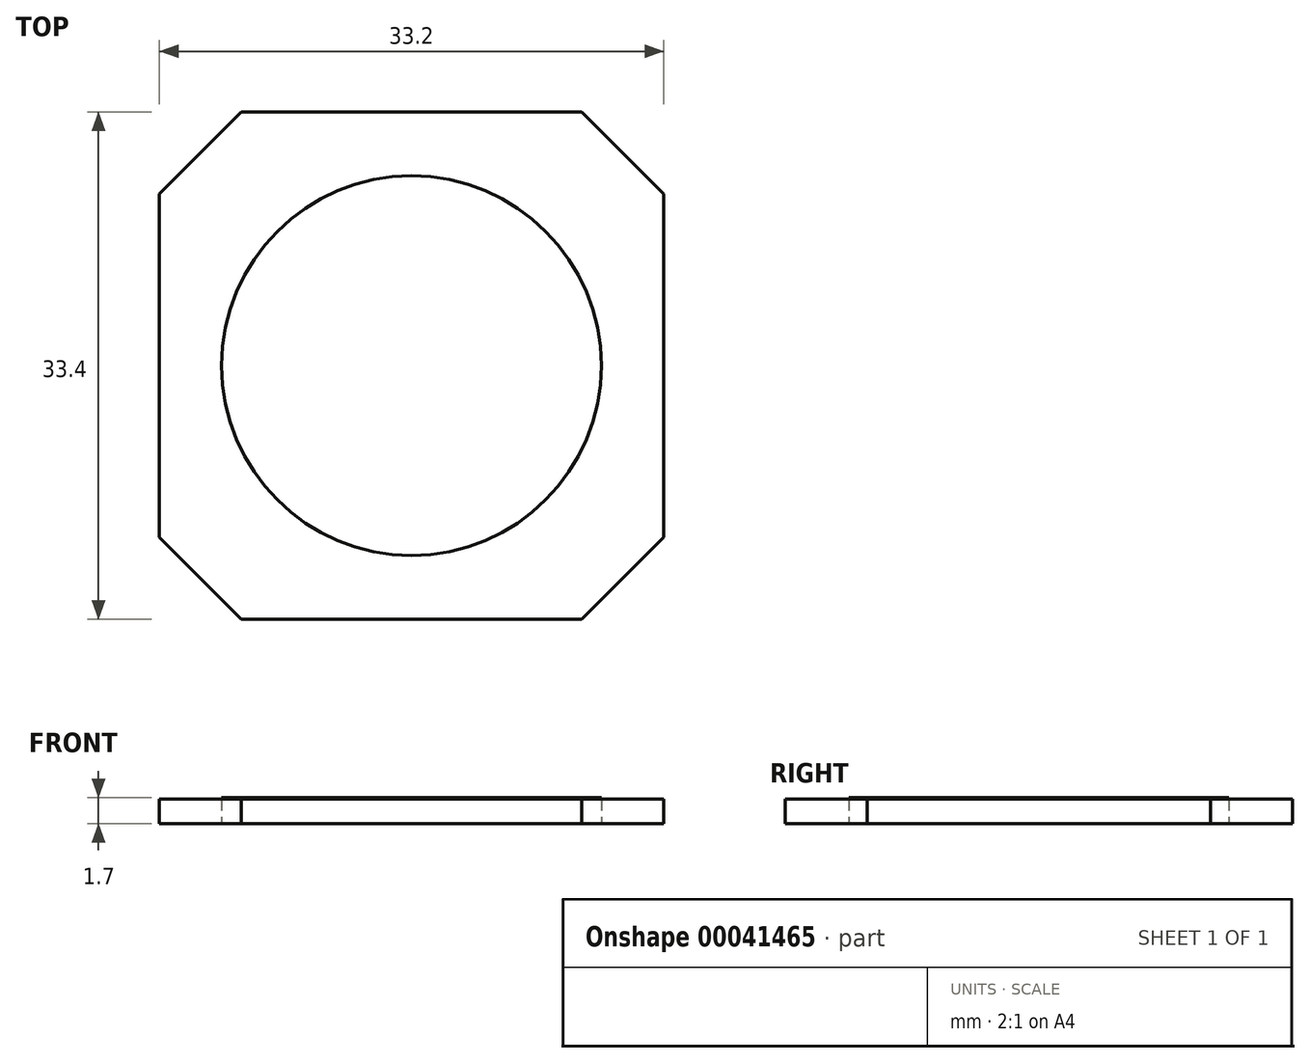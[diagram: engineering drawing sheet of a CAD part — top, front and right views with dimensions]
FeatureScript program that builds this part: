
annotation { "Feature Type Name" : "Feature", "Feature Type Description" : "" }
export const myFeature = defineFeature(function(context is Context, id is Id, definition is map)
    precondition{}
    {
        {
            var Q0;
            Q0=qCreatedBy(makeId("Top.planeOp"),FACE);
            var sketch = newSketch(context, id + "F0", { "sketchPlane" : qUnion([Q0])});
            skCircle(sketch, "E0", {"center": v(0, 0) * mm, "radius": 12.5 * mm, "construction": true});
            skLineSegment(sketch, "E1.bottom", {"start": v(-11.2, 16.7) * mm, "end": v(11.2, 16.7) * mm});
            skLineSegment(sketch, "E1.top", {"start": v(-11.2, -16.7) * mm, "end": v(11.2, -16.7) * mm});
            skLineSegment(sketch, "E1.left", {"start": v(-16.6, 11.3) * mm, "end": v(-16.6, -11.3) * mm});
            skLineSegment(sketch, "E1.right", {"start": v(16.6, 11.3) * mm, "end": v(16.6, -11.3) * mm});
            skLineSegment(sketch, "E2", {"start": v(0, 16.7) * mm, "end": v(0, 0) * mm, "construction": true});
            skLineSegment(sketch, "E3", {"start": v(0, 0) * mm, "end": v(-16.6, 0) * mm, "construction": true});
            skLineSegment(sketch, "E4", {"start": v(-11.2, 16.7) * mm, "end": v(-16.6, 11.3) * mm});
            skLineSegment(sketch, "E5.MirrorCS", {"start": v(11.2, 16.7) * mm, "end": v(16.6, 11.3) * mm});
            skLineSegment(sketch, "E6.MirrorCS", {"start": v(-11.2, -16.7) * mm, "end": v(-16.6, -11.3) * mm});
            skLineSegment(sketch, "E7.MirrorCS", {"start": v(11.2, -16.7) * mm, "end": v(16.6, -11.3) * mm});
            skPoint(sketch, "E8.orphan", {"position": v(-16.6, 16.7) * mm});
            skPoint(sketch, "E9.orphan", {"position": v(-16.6, -16.7) * mm});
            skPoint(sketch, "E10.orphan", {"position": v(16.6, 16.7) * mm});
            skSolve(sketch);
        }
        {
            var Q0;
            Q0=makeQuery(id+"F0.imprint","IMPRINT",FACE,{"disambiguationData":[TD([[makeQuery(id+"F0.imprint","IMPRINT",EDGE,{"derivedFrom":sQuery(id+"F0.wireOp",EDGE,"E1.bottom")}),-1.0]])]});
            var Q1;
            Q1=sQuery(id+"F0.wireOp",EDGE,"E1.bottom");
            var Q2;
            Q2=sQuery(id+"F0.wireOp",EDGE,"E4");
            var Q3;
            Q3=sQuery(id+"F0.wireOp",EDGE,"E1.left");
            var Q4;
            Q4=sQuery(id+"F0.wireOp",EDGE,"E6.MirrorCS");
            var Q5;
            Q5=sQuery(id+"F0.wireOp",EDGE,"E1.top");
            var Q6;
            Q6=sQuery(id+"F0.wireOp",EDGE,"E7.MirrorCS");
            var Q7;
            Q7=sQuery(id+"F0.wireOp",EDGE,"E1.right");
            var Q8;
            Q8=sQuery(id+"F0.wireOp",EDGE,"E5.MirrorCS");
            extrude(context, id + "F1", {"entities" : qUnion([Q0]), "surfaceEntities" : qUnion([Q1, Q2, Q3, Q4, Q5, Q6, Q7, Q8]), "depth" : 1.6 * mm});
        }
        {
            var Q0;
            Q0=qCreatedBy(makeId("Top.planeOp"),FACE);
            var sketch = newSketch(context, id + "F2", { "sketchPlane" : qUnion([Q0])});
            skCircle(sketch, "E11", {"center": v(0, 0) * mm, "radius": 12.5 * mm});
            skSolve(sketch);
        }
        {
            var Q0;
            Q0 = qSketchRegion(id + "F2", true);
            extrude(context, id + "F3", {"entities" : qUnion([Q0]), "depth" : 1.7 * mm});
        }
    });
